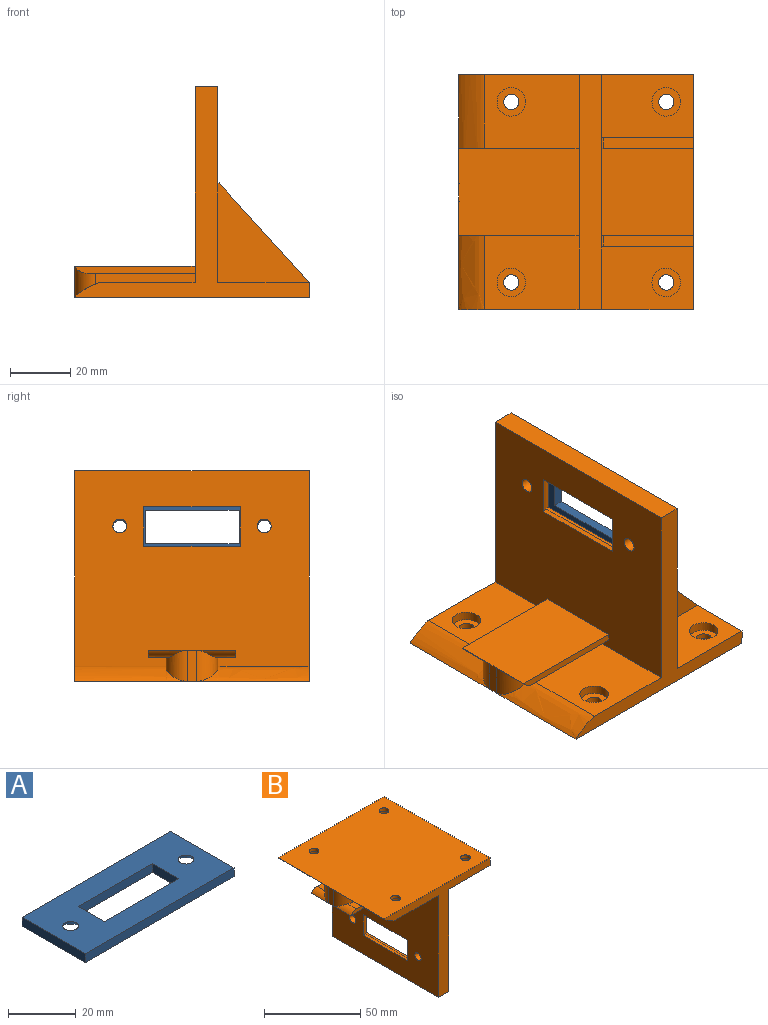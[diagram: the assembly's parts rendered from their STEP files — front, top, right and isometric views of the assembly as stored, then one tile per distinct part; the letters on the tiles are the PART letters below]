
ASSEMBLY  parts=2 mates=1
PART A: 12 faces, bbox 62x26.3x3.2 mm
  f0: plane 62x26.3mm, normal (0,0,-1), area 1099.5mm2, adj f2,f3,f4,f5,f6,f7,f8,f9
  f1: plane 62x26.3mm, normal (0,0,1), area 1256.4mm2, adj f2,f3,f4,f5,f6,f7,f8,f9
  f2: plane 62x3.2mm, normal (0,1,0), area 198.4mm2, adj f0,f1,f3,f5
  f3: plane 26.3x3.2mm, normal (-1,0,0), area 84.2mm2, adj f0,f1,f2,f4
  f4: plane 62x3.2mm, normal (0,-1,0), area 198.4mm2, adj f0,f1,f3,f5
  f5: plane 26.3x3.2mm, normal (1,0,0), area 84.2mm2, adj f0,f1,f2,f4
  f6: cone r=2.3mm half-angle=45deg, axis (0,0,-1), area 110.9mm2, adj f0,f1
  f7: cone r=5.5mm half-angle=45deg, axis (0,0,-1), area 110.9mm2, adj f0,f1
  f8: plane 31x3.2mm, normal (0,1,0), area 99.2mm2, adj f0,f1,f9,f11
  f9: plane 11x3.2mm, normal (1,0,0), area 35.2mm2, adj f0,f1,f8,f10
  f10: plane 31x3.2mm, normal (0,-1,0), area 99.2mm2, adj f0,f1,f9,f11
  f11: plane 11x3.2mm, normal (-1,0,0), area 35.2mm2, adj f0,f1,f8,f10
PART B: 61 faces, bbox 78.4x81.4x70.4 mm
  f0: plane 78x65mm, normal (-1,0,0), area 4496.5mm2, adj f4,f5,f8,f9,f10,f11,f13,f14
  f1: plane 62.2x26.3mm, normal (1,0,0), area 1041.5mm2, adj f39,f40,f41,f42,f43,f44,f45,f46
  f2: plane 30.5x21mm, normal (0,0,-1), area 569.6mm2, adj f17,f18,f27,f38,f50
  f3: plane 30.5x29mm, normal (0,0,-1), area 884.5mm2, adj f17,f38,f48,f51
  f4: plane 31.34x30.38mm, normal (0,0,-1), area 881.1mm2, adj f0,f15,f16,f20,f23
  f5: plane 31.34x30.38mm, normal (0,0,-1), area 881.1mm2, adj f0,f14,f18,f19,f29
  f6: plane 78x78mm, normal (0,0,1), area 6002.3mm2, adj f12,f16,f17,f18,f19,f20,f31,f32
  f7: plane 30.5x21mm, normal (0,0,-1), area 569.6mm2, adj f16,f17,f25,f38,f47
  f8: plane 35.79x6.46mm, normal (0,0,1), area 210.8mm2, adj f0,f11,f14,f21,f36
  f9: plane 35.79x6.46mm, normal (0,0,1), area 210.8mm2, adj f0,f10,f15,f22,f35
  f10: plane 40x2.3mm, normal (0,-1,0), area 89.1mm2, adj f0,f9,f13,f35
  f11: plane 40x2.3mm, normal (0,1,0), area 89.1mm2, adj f0,f8,f13,f36
  f12: plane 10.3x3.25mm, normal (-1,0,0), area 33.5mm2, adj f6,f13,f21,f22
  f13: plane 40x29mm, normal (0,0,-1), area 1160mm2, adj f0,f10,f11,f12,f35,f36
  f14: plane 33.36x3.86mm, normal (0,1,0), area 99.3mm2, adj f0,f5,f8,f19,f21
  f15: plane 33.43x3.93mm, normal (0,-1,0), area 99.3mm2, adj f0,f4,f9,f20,f22
  f16: plane 78x70mm, normal (0,-1,0), area 857.6mm2, adj f0,f4,f6,f7,f17,f20,f37,f38
  f17: plane 78x5mm, normal (1,0,0), area 390mm2, adj f2,f3,f6,f7,f16,f18,f53,f54
  f18: plane 78x70mm, normal (0,1,0), area 857.3mm2, adj f0,f2,f5,f6,f17,f19,f37,f38
  f19: bspline ~39.12x8.66mm, area 321.2mm2, adj f5,f6,f14,f18,f21
  f20: bspline ~39.12x8.66mm, area 321.2mm2, adj f4,f6,f15,f16,f22
  f21: cylinder r=7mm len=10.3mm, axis (0,0,1), area 72.6mm2, adj f8,f12,f14,f19,f36
  f22: cylinder r=7mm len=10.3mm, axis (0,0,1), area 72.6mm2, adj f9,f12,f15,f20,f35
  f23: cylinder r=4.75mm len=9.5mm, axis (0,0,-1), area 89.5mm2, adj f4,f24
  f24: plane 9.5x9.5mm, normal (0,0,-1), area 50.5mm2, adj f23,f34
  f25: cylinder r=4.75mm len=9.5mm, axis (0,0,-1), area 89.5mm2, adj f7,f26
  f26: plane 9.5x9.5mm, normal (0,0,-1), area 50.5mm2, adj f25,f33
  f27: cylinder r=4.75mm len=9.5mm, axis (0,0,-1), area 89.5mm2, adj f2,f28
  f28: plane 9.5x9.5mm, normal (0,0,-1), area 50.5mm2, adj f27,f32
  f29: cylinder r=4.75mm len=9.5mm, axis (0,0,-1), area 89.5mm2, adj f5,f30
  f30: plane 9.5x9.5mm, normal (0,0,-1), area 50.5mm2, adj f29,f31
  f31: cylinder r=2.55mm len=5.1mm, axis (0,0,-1), area 32mm2, adj f6,f30
  f32: cylinder r=2.55mm len=5.1mm, axis (0,0,-1), area 32mm2, adj f6,f28
  f33: cylinder r=2.55mm len=5.1mm, axis (0,0,-1), area 32mm2, adj f6,f26
  f34: cylinder r=2.55mm len=5.1mm, axis (0,0,-1), area 32mm2, adj f6,f24
  f35: cylinder r=5mm len=12.88mm, axis (0,-1,0), area 48.3mm2, adj f9,f10,f13,f22
  f36: cylinder r=5mm len=12.88mm, axis (0,-1,0), area 48.3mm2, adj f8,f11,f13,f21
  f37: plane 78x7.5mm, normal (0,0,-1), area 585mm2, adj f0,f16,f18,f38
  f38: plane 78x65mm, normal (1,0,0), area 3203.1mm2, adj f2,f3,f7,f16,f18,f37,f39,f40
  f39: plane 62.2x3.2mm, normal (0,0,1), area 199mm2, adj f1,f38,f40,f42
  f40: plane 26.3x3.2mm, normal (0,-1,0), area 84.2mm2, adj f1,f38,f39,f41
  f41: plane 62.2x3.2mm, normal (0,0,-1), area 199mm2, adj f1,f38,f40,f42
  f42: plane 26.3x3.2mm, normal (0,1,0), area 84.2mm2, adj f1,f38,f39,f41
  f43: plane 15.5x1.3mm, normal (0,-1,0), area 20.2mm2, adj f1,f44,f46,f57
  f44: plane 36.2x1.3mm, normal (0,0,-1), area 47.1mm2, adj f1,f43,f45,f60
  f45: plane 15.5x1.3mm, normal (0,1,0), area 20.2mm2, adj f1,f44,f46,f58
  f46: plane 36.2x1.3mm, normal (0,0,1), area 47.1mm2, adj f1,f43,f45,f59
  f47: plane 33x30.5mm, normal (0,-1,0), area 511.5mm2, adj f7,f38,f49,f53
  f48: plane 33x30.5mm, normal (0,1,0), area 511.5mm2, adj f3,f38,f49,f53
  f49: plane 3.5x0.5mm, normal (0,0,-1), area 1.8mm2, adj f38,f47,f48,f53
  f50: plane 33x30.5mm, normal (0,1,0), area 511.5mm2, adj f2,f38,f52,f54
  f51: plane 33x30.5mm, normal (0,-1,0), area 511.5mm2, adj f3,f38,f52,f54
  f52: plane 3.5x0.5mm, normal (0,0,-1), area 1.7mm2, adj f38,f50,f51,f54
  f53: plane 33x30mm, normal (0.74,0,-0.67), area 156.1mm2, adj f17,f47,f48,f49
  f54: plane 33x30mm, normal (0.74,0,-0.67), area 156.1mm2, adj f17,f50,f51,f52
  f55: cylinder r=2.3mm len=4.6mm, axis (1,0,0), area 62.1mm2, adj f0,f1
  f56: cylinder r=2.3mm len=4.6mm, axis (1,0,0), area 62.1mm2, adj f0,f1
  f57: plane 15.5x3mm, normal (0.55,-0.83,0), area 51.6mm2, adj f0,f43,f59,f60
  f58: plane 15.5x3mm, normal (0.55,0.83,0), area 51.6mm2, adj f0,f45,f59,f60
  f59: plane 36.2x3mm, normal (0.37,0,0.93), area 110.5mm2, adj f0,f46,f57,f58
  f60: plane 36.2x3mm, normal (0.37,0,-0.93), area 110.5mm2, adj f0,f44,f57,f58
PLACE A rot(axis=(0.58,-0.58,-0.58),120deg) t=(13.15,-188.44,5.7)mm
PLACE B rot(axis=(1,0,0),180deg) t=(63.55,-44.17,-43.61)mm
MATE planar B.f1 <-> A.f1  axis (1,0,0) through (2.85,-44.17,-2.46)mm
